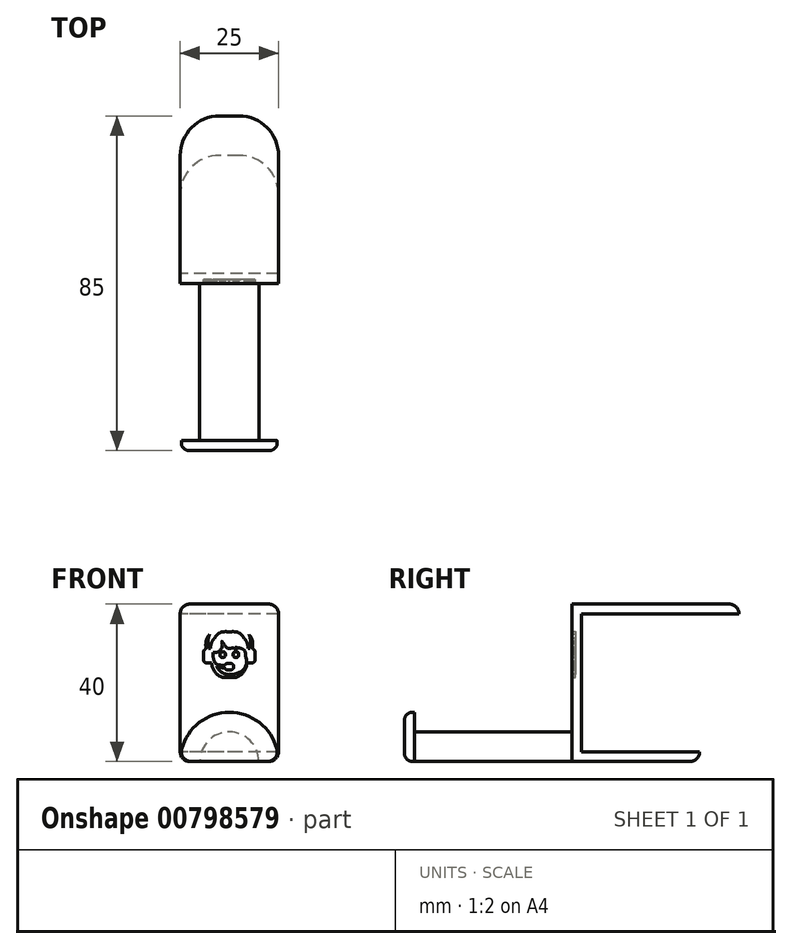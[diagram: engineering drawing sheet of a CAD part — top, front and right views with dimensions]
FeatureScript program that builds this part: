
annotation { "Feature Type Name" : "Feature", "Feature Type Description" : "" }
export const myFeature = defineFeature(function(context is Context, id is Id, definition is map)
    precondition{}
    {
        {
            var Q0;
            Q0=qCreatedBy(makeId("Right.planeOp"),FACE);
            var sketch = newSketch(context, id + "F0", { "sketchPlane" : qUnion([Q0])});
            skLineSegment(sketch, "E0", {"start": v(0, 0) * mm, "end": v(0, 35) * mm});
            skLineSegment(sketch, "E1", {"start": v(0, 35) * mm, "end": v(40, 35) * mm});
            skLineSegment(sketch, "E2", {"start": v(0, 0) * mm, "end": v(30, 0) * mm});
            skLineSegment(sketch, "E3.0", {"start": v(-2.5, 37.5) * mm, "end": v(40, 37.5) * mm});
            skLineSegment(sketch, "E3.1", {"start": v(-2.5, -2.5) * mm, "end": v(-2.5, 37.5) * mm});
            skLineSegment(sketch, "E3.2", {"start": v(-2.5, -2.5) * mm, "end": v(30, -2.5) * mm});
            skLineSegment(sketch, "E4", {"start": v(30, 0) * mm, "end": v(30, -2.5) * mm});
            skLineSegment(sketch, "E5", {"start": v(40, 35) * mm, "end": v(40, 37.5) * mm});
            skSolve(sketch);
        }
        {
            var Q0;
            Q0=makeQuery(id+"F0.imprint","IMPRINT",FACE,{"disambiguationData":[TD([[makeQuery(id+"F0.imprint","IMPRINT",EDGE,{"derivedFrom":sQuery(id+"F0.wireOp",EDGE,"E0")}),1.0]])]});
            extrude(context, id + "F1", {"entities" : qUnion([Q0]), "depth" : 25 * mm, "offsetDistance" : 25 * mm});
        }
        {
            var Q0;
            Q0=makeQuery(id+"F1.opExtrude","CAP_EDGE",EDGE,{"disambiguationData":[OSD([sQuery(id+"F0.wireOp",EDGE,"E5")])],"isStart":true});
            var Q1;
            Q1=makeQuery(id+"F1.opExtrude","CAP_EDGE",EDGE,{"disambiguationData":[OSD([sQuery(id+"F0.wireOp",EDGE,"E5")])],"isStart":false});
            var Q2;
            Q2=makeQuery(id+"F1.opExtrude","CAP_EDGE",EDGE,{"disambiguationData":[OSD([sQuery(id+"F0.wireOp",EDGE,"E4")])],"isStart":false});
            var Q3;
            Q3=makeQuery(id+"F1.opExtrude","CAP_EDGE",EDGE,{"disambiguationData":[OSD([sQuery(id+"F0.wireOp",EDGE,"E4")])],"isStart":true});
            fillet(context, id + "F2", {"entities" : qUnion([Q0, Q1, Q2, Q3]), "radius" : 10 * mm, "tangentPropagation" : true, "allowEdgeOverflow" : false});
        }
        {
            var Q0;
            Q0=makeQuery(id+"F2.opFillet","BLEND_EDGE",EDGE,{"blendedFrom":[makeQuery(id+"F1.opExtrude","CAP_EDGE",EDGE,{"disambiguationData":[OSD([sQuery(id+"F0.wireOp",EDGE,"E5")])],"isStart":true}),makeQuery(id+"F1.opExtrude","SWEPT_FACE",FACE,{"disambiguationData":[OSD([sQuery(id+"F0.wireOp",EDGE,"E3.0")])]})],"blendedInto":[makeQuery(id+"F1.opExtrude","SWEPT_FACE",FACE,{"disambiguationData":[OSD([sQuery(id+"F0.wireOp",EDGE,"E3.0")])]})]});
            var Q1;
            Q1=makeQuery(id+"F1.opExtrude","SWEPT_EDGE",EDGE,{"disambiguationData":[OSD([sQuery(id+"F0.wireOp",EDGE,"E3.0"),sQuery(id+"F0.wireOp",EDGE,"E5")])]});
            var Q2;
            Q2=makeQuery(id+"F2.opFillet","BLEND_EDGE",EDGE,{"blendedFrom":[makeQuery(id+"F1.opExtrude","CAP_EDGE",EDGE,{"disambiguationData":[OSD([sQuery(id+"F0.wireOp",EDGE,"E5")])],"isStart":false}),makeQuery(id+"F1.opExtrude","SWEPT_FACE",FACE,{"disambiguationData":[OSD([sQuery(id+"F0.wireOp",EDGE,"E3.0")])]})],"blendedInto":[makeQuery(id+"F1.opExtrude","SWEPT_FACE",FACE,{"disambiguationData":[OSD([sQuery(id+"F0.wireOp",EDGE,"E3.0")])]})]});
            var Q3;
            Q3=makeQuery(id+"F2.opFillet","BLEND_EDGE",EDGE,{"blendedFrom":[makeQuery(id+"F1.opExtrude","CAP_EDGE",EDGE,{"disambiguationData":[OSD([sQuery(id+"F0.wireOp",EDGE,"E4")])],"isStart":true}),makeQuery(id+"F1.opExtrude","SWEPT_FACE",FACE,{"disambiguationData":[OSD([sQuery(id+"F0.wireOp",EDGE,"E3.2")])]})],"blendedInto":[makeQuery(id+"F1.opExtrude","SWEPT_FACE",FACE,{"disambiguationData":[OSD([sQuery(id+"F0.wireOp",EDGE,"E3.2")])]})]});
            var Q4;
            Q4=makeQuery(id+"F1.opExtrude","SWEPT_EDGE",EDGE,{"disambiguationData":[OSD([sQuery(id+"F0.wireOp",EDGE,"E3.2"),sQuery(id+"F0.wireOp",EDGE,"E4")])]});
            var Q5;
            Q5=makeQuery(id+"F2.opFillet","BLEND_EDGE",EDGE,{"blendedFrom":[makeQuery(id+"F1.opExtrude","CAP_EDGE",EDGE,{"disambiguationData":[OSD([sQuery(id+"F0.wireOp",EDGE,"E4")])],"isStart":false}),makeQuery(id+"F1.opExtrude","SWEPT_FACE",FACE,{"disambiguationData":[OSD([sQuery(id+"F0.wireOp",EDGE,"E3.2")])]})],"blendedInto":[makeQuery(id+"F1.opExtrude","SWEPT_FACE",FACE,{"disambiguationData":[OSD([sQuery(id+"F0.wireOp",EDGE,"E3.2")])]})]});
            fillet(context, id + "F3", {"entities" : qUnion([Q0, Q1, Q2, Q3, Q4, Q5]), "radius" : 2.5 * mm, "tangentPropagation" : true, "allowEdgeOverflow" : false});
        }
        {
            var Q0;
            Q0=makeQuery(id+"F1.opExtrude","SWEPT_FACE",FACE,{"disambiguationData":[OSD([sQuery(id+"F0.wireOp",EDGE,"E3.1")])]});
            var sketch = newSketch(context, id + "F4", { "sketchPlane" : qUnion([Q0])});
            skCircle(sketch, "E6", {"center": v(12.5, -2.5) * mm, "radius": 7.5 * mm});
            skSolve(sketch);
        }
        {
            var Q0;
            {var subQ0=sQuery(id+"F4.wireOp",EDGE,"E6");var subQ1=makeQuery(id+"F1.opExtrude","SWEPT_EDGE",EDGE,{"disambiguationData":[OSD([sQuery(id+"F0.wireOp",EDGE,"E3.1"),sQuery(id+"F0.wireOp",EDGE,"E3.2")])]});var subQ2=makeQuery(id+"F4.imprint","INTERSECT",VERTEX,{"disambiguationData":[OD(0.0)],"derivedFrom":[subQ1,subQ0]});Q0=makeQuery(id+"F4.imprint","IMPRINT",FACE,{"disambiguationData":[TD([[makeQuery(id+"F4.imprint","IMPRINT",EDGE,{"disambiguationData":[TD([[subQ2,1.0]])],"derivedFrom":subQ0}),1.0]])]});}
            extrude(context, id + "F5", {"entities" : qUnion([Q0]), "operationType" : NewBodyOperationType.ADD, "depth" : 40 * mm, "offsetDistance" : 25 * mm});
        }
        {
            var Q0;
            Q0=makeQuery(id+"F5.opExtrude","CAP_FACE",FACE,{"disambiguationData":[OSD([sQuery(id+"F0.wireOp",EDGE,"E3.1"),sQuery(id+"F0.wireOp",EDGE,"E3.2"),sQuery(id+"F4.wireOp",EDGE,"E6")])],"isStart":false});
            var sketch = newSketch(context, id + "F6", { "sketchPlane" : qUnion([Q0])});
            skCircle(sketch, "E7", {"center": v(12.5, -2.5) * mm, "radius": 12.5 * mm});
            skLineSegment(sketch, "E8", {"start": v(12.5, -2.5) * mm, "end": v(25, -2.5) * mm});
            skLineSegment(sketch, "E9", {"start": v(12.5, -2.5) * mm, "end": v(0, -2.5) * mm});
            skSolve(sketch);
        }
        {
            var Q0;
            {var subQ1=makeQuery(id+"F5.opExtrude","CAP_EDGE",EDGE,{"disambiguationData":[OSD([sQuery(id+"F4.wireOp",EDGE,"E6")])],"isStart":false});Q0=makeQuery(id+"F6.imprint","IMPRINT",FACE,{"disambiguationData":[TD([[makeQuery(id+"F6.imprint","IMPRINT",EDGE,{"derivedFrom":subQ1}),1.0]])]});}
            var Q1;
            {var subQ5=makeQuery(id+"F5.opExtrude","CAP_EDGE",EDGE,{"disambiguationData":[OSD([sQuery(id+"F4.wireOp",EDGE,"E6")])],"isStart":false});Q1=makeQuery(id+"F6.imprint","IMPRINT",FACE,{"disambiguationData":[TD([[makeQuery(id+"F6.imprint","IMPRINT",EDGE,{"derivedFrom":subQ5}),-1.0]])]});}
            extrude(context, id + "F7", {"entities" : qUnion([Q0, Q1]), "operationType" : NewBodyOperationType.ADD, "depth" : 2.5 * mm, "offsetDistance" : 25 * mm});
        }
        {
            var Q0;
            Q0=makeQuery(id+"F7.opExtrude","SWEPT_EDGE",EDGE,{"disambiguationData":[OSD([sQuery(id+"F6.wireOp",EDGE,"E7"),sQuery(id+"F6.wireOp",EDGE,"E9")])]});
            var Q1;
            Q1=makeQuery(id+"F7.opExtrude","SWEPT_EDGE",EDGE,{"disambiguationData":[OSD([sQuery(id+"F6.wireOp",EDGE,"E7"),sQuery(id+"F6.wireOp",EDGE,"E8")])]});
            fillet(context, id + "F8", {"entities" : qUnion([Q0, Q1]), "radius" : 2.5 * mm, "tangentPropagation" : true, "allowEdgeOverflow" : false});
        }
        {
            var Q0;
            Q0=makeQuery(id+"F7.opExtrude","CAP_EDGE",EDGE,{"disambiguationData":[OSD([sQuery(id+"F6.wireOp",EDGE,"E7")])],"isStart":false});
            var Q1;
            Q1=makeQuery(id+"F5.opExtrude","CAP_EDGE",EDGE,{"disambiguationData":[OSD([sQuery(id+"F4.wireOp",EDGE,"E6")])],"isStart":false});
            var Q2;
            Q2=makeQuery(id+"F5.opExtrude","CAP_EDGE",EDGE,{"disambiguationData":[OSD([sQuery(id+"F4.wireOp",EDGE,"E6")])],"isStart":true});
            fillet(context, id + "F9", {"entities" : qUnion([Q0, Q1, Q2]), "radius" : 2 * mm, "tangentPropagation" : true, "allowEdgeOverflow" : false});
        }
        {
            var Q0;
            Q0=makeQuery(id+"F1.opExtrude","SWEPT_FACE",FACE,{"disambiguationData":[OSD([sQuery(id+"F0.wireOp",EDGE,"E3.1")])]});
            var sketch = newSketch(context, id + "F10", { "sketchPlane" : qUnion([Q0])});
            skFitSpline(sketch, "E10", {"points": [v(11.46, 24.67) * mm, v(11.46, 24.3) * mm, v(11.16, 24) * mm, v(10.8, 24) * mm]});
            skFitSpline(sketch, "E11", {"points": [v(10.8, 24) * mm, v(10.42, 24) * mm, v(10.12, 24.3) * mm, v(10.12, 24.67) * mm]});
            skFitSpline(sketch, "E12", {"points": [v(10.12, 24.67) * mm, v(10.12, 25.04) * mm, v(10.42, 25.34) * mm, v(10.8, 25.34) * mm]});
            skFitSpline(sketch, "E13", {"points": [v(10.8, 25.34) * mm, v(11.16, 25.34) * mm, v(11.46, 25.04) * mm, v(11.46, 24.67) * mm]});
            skFitSpline(sketch, "E14", {"points": [v(14.2, 25.34) * mm, v(13.82, 25.34) * mm, v(13.52, 25.04) * mm, v(13.52, 24.67) * mm]});
            skFitSpline(sketch, "E15", {"points": [v(13.52, 24.67) * mm, v(13.52, 24.3) * mm, v(13.82, 24) * mm, v(14.2, 24) * mm]});
            skFitSpline(sketch, "E16", {"points": [v(14.2, 24) * mm, v(14.56, 24) * mm, v(14.86, 24.3) * mm, v(14.86, 24.67) * mm]});
            skFitSpline(sketch, "E17", {"points": [v(14.86, 24.67) * mm, v(14.86, 25.04) * mm, v(14.56, 25.34) * mm, v(14.2, 25.34) * mm]});
            skLineSegment(sketch, "E18", {"start": v(19.03, 25.04) * mm, "end": v(19.03, 23.76) * mm});
            skFitSpline(sketch, "E19", {"points": [v(19.03, 23.76) * mm, v(19.03, 23.12) * mm, v(18.51, 22.6) * mm, v(17.87, 22.6) * mm]});
            skLineSegment(sketch, "E20", {"start": v(17.87, 22.6) * mm, "end": v(17.03, 22.6) * mm});
            skFitSpline(sketch, "E21", {"points": [v(17.03, 22.6) * mm, v(16.2, 20.29) * mm, v(14.07, 18.89) * mm, v(12.5, 18.89) * mm]});
            skFitSpline(sketch, "E22", {"points": [v(12.5, 18.89) * mm, v(10.92, 18.89) * mm, v(8.79, 20.29) * mm, v(7.95, 22.6) * mm]});
            skLineSegment(sketch, "E23", {"start": v(7.95, 22.6) * mm, "end": v(7.11, 22.6) * mm});
            skFitSpline(sketch, "E24", {"points": [v(7.11, 22.6) * mm, v(6.47, 22.6) * mm, v(5.95, 23.12) * mm, v(5.95, 23.76) * mm]});
            skLineSegment(sketch, "E25", {"start": v(5.95, 23.76) * mm, "end": v(5.95, 25.04) * mm});
            skFitSpline(sketch, "E26", {"points": [v(5.95, 25.04) * mm, v(5.95, 25.48) * mm, v(6.2, 25.87) * mm, v(6.56, 26.06) * mm]});
            skFitSpline(sketch, "E27", {"points": [v(6.56, 26.06) * mm, v(6.57, 27.87) * mm, v(7.1, 29.29) * mm, v(8.13, 30.27) * mm]});
            skFitSpline(sketch, "E28", {"points": [v(8.13, 30.27) * mm, v(9.16, 31.24) * mm, v(10.62, 31.73) * mm, v(12.5, 31.73) * mm]});
            skFitSpline(sketch, "E29", {"points": [v(12.5, 31.73) * mm, v(14.36, 31.73) * mm, v(15.83, 31.24) * mm, v(16.85, 30.27) * mm]});
            skFitSpline(sketch, "E30", {"points": [v(16.85, 30.27) * mm, v(17.88, 29.29) * mm, v(18.41, 27.87) * mm, v(18.42, 26.06) * mm]});
            skFitSpline(sketch, "E31", {"points": [v(18.42, 26.06) * mm, v(18.79, 25.87) * mm, v(19.03, 25.48) * mm, v(19.03, 25.04) * mm]});
            skFitSpline(sketch, "E32", {"points": [v(16.58, 24.66) * mm, v(16.58, 24.96) * mm, v(16.56, 25.24) * mm, v(16.54, 25.51) * mm]});
            skFitSpline(sketch, "E33", {"points": [v(16.54, 25.51) * mm, v(16.02, 25.98) * mm, v(15.09, 26.34) * mm, v(13.9, 26.47) * mm]});
            skFitSpline(sketch, "E34", {"points": [v(13.9, 26.47) * mm, v(14.06, 26.3) * mm, v(14.2, 26.07) * mm, v(14.28, 25.77) * mm]});
            skFitSpline(sketch, "E35", {"points": [v(14.28, 25.77) * mm, v(13.56, 26.34) * mm, v(12.14, 26.2) * mm, v(11.06, 27.48) * mm]});
            skFitSpline(sketch, "E36", {"points": [v(11.06, 27.48) * mm, v(11, 27.55) * mm, v(10.95, 27.62) * mm, v(10.9, 27.68) * mm]});
            skFitSpline(sketch, "E37", {"points": [v(10.9, 27.68) * mm, v(10.9, 27.68) * mm, v(10.9, 27.68) * mm, v(10.9, 27.68) * mm]});
            skLineSegment(sketch, "E38", {"start": v(10.9, 27.68) * mm, "end": v(10.9, 27.68) * mm});
            skFitSpline(sketch, "E39", {"points": [v(10.9, 27.68) * mm, v(10.71, 27.94) * mm, v(10.65, 28.1) * mm, v(10.64, 27.92) * mm]});
            skFitSpline(sketch, "E40", {"points": [v(10.64, 27.92) * mm, v(10.61, 26.46) * mm, v(9.57, 25.32) * mm, v(8.42, 25.16) * mm]});
            skFitSpline(sketch, "E41", {"points": [v(8.42, 25.16) * mm, v(8.41, 25) * mm, v(8.4, 24.83) * mm, v(8.4, 24.66) * mm]});
            skFitSpline(sketch, "E42", {"points": [v(8.4, 24.66) * mm, v(8.4, 24.04) * mm, v(8.5, 23.48) * mm, v(8.68, 22.97) * mm]});
            skFitSpline(sketch, "E43", {"points": [v(8.68, 22.97) * mm, v(9.33, 22.19) * mm, v(10.4, 21.97) * mm, v(11.34, 21.91) * mm]});
            skFitSpline(sketch, "E44", {"points": [v(11.34, 21.91) * mm, v(11.52, 22.2) * mm, v(11.91, 22.39) * mm, v(12.37, 22.39) * mm]});
            skFitSpline(sketch, "E45", {"points": [v(12.37, 22.39) * mm, v(13, 22.39) * mm, v(13.5, 22.03) * mm, v(13.5, 21.59) * mm]});
            skFitSpline(sketch, "E46", {"points": [v(13.5, 21.59) * mm, v(13.5, 21.14) * mm, v(13, 20.79) * mm, v(12.37, 20.79) * mm]});
            skFitSpline(sketch, "E47", {"points": [v(12.37, 20.79) * mm, v(11.9, 20.79) * mm, v(11.49, 21) * mm, v(11.32, 21.3) * mm]});
            skFitSpline(sketch, "E48", {"points": [v(11.32, 21.3) * mm, v(10.66, 21.34) * mm, v(9.93, 21.45) * mm, v(9.29, 21.75) * mm]});
            skFitSpline(sketch, "E49", {"points": [v(9.29, 21.75) * mm, v(10.2, 20.41) * mm, v(11.61, 19.7) * mm, v(12.5, 19.7) * mm]});
            skFitSpline(sketch, "E50", {"points": [v(12.5, 19.7) * mm, v(13.88, 19.7) * mm, v(16.58, 21.45) * mm, v(16.58, 24.66) * mm]});
            skLineSegment(sketch, "E51", {"start": v(16.58, 24.66) * mm, "end": v(16.58, 24.66) * mm});
            skFitSpline(sketch, "E52", {"points": [v(17.73, 26.2) * mm, v(17.65, 29.36) * mm, v(15.85, 31.03) * mm, v(12.5, 31.03) * mm]});
            skFitSpline(sketch, "E53", {"points": [v(12.5, 31.03) * mm, v(9.14, 31.03) * mm, v(7.33, 29.36) * mm, v(7.26, 26.2) * mm]});
            skLineSegment(sketch, "E54", {"start": v(7.26, 26.2) * mm, "end": v(7.7, 26.2) * mm});
            skFitSpline(sketch, "E55", {"points": [v(7.7, 26.2) * mm, v(7.87, 27.27) * mm, v(8.21, 28.14) * mm, v(8.74, 28.82) * mm]});
            skFitSpline(sketch, "E56", {"points": [v(8.74, 28.82) * mm, v(9.57, 29.9) * mm, v(10.84, 30.44) * mm, v(12.5, 30.44) * mm]});
            skFitSpline(sketch, "E57", {"points": [v(12.5, 30.44) * mm, v(14.15, 30.44) * mm, v(15.41, 29.9) * mm, v(16.25, 28.82) * mm]});
            skFitSpline(sketch, "E58", {"points": [v(16.25, 28.82) * mm, v(16.77, 28.14) * mm, v(17.12, 27.27) * mm, v(17.28, 26.2) * mm]});
            skLineSegment(sketch, "E59", {"start": v(17.28, 26.2) * mm, "end": v(17.73, 26.2) * mm});
            skSolve(sketch);
        }
        {
            var Q0;
            Q0=makeQuery(id+"F10.imprint","IMPRINT",FACE,{"disambiguationData":[TD([[makeQuery(id+"F10.imprint","IMPRINT",EDGE,{"derivedFrom":sQuery(id+"F10.wireOp",EDGE,"E18")}),-1.0]])]});
            var Q1;
            Q1=makeQuery(id+"F10.imprint","IMPRINT",FACE,{"disambiguationData":[TD([[makeQuery(id+"F10.imprint","IMPRINT",EDGE,{"derivedFrom":sQuery(id+"F10.wireOp",EDGE,"E14")}),1.0]])]});
            var Q2;
            Q2=makeQuery(id+"F10.imprint","IMPRINT",FACE,{"disambiguationData":[TD([[makeQuery(id+"F10.imprint","IMPRINT",EDGE,{"derivedFrom":sQuery(id+"F10.wireOp",EDGE,"E10")}),-1.0]])]});
            extrude(context, id + "F11", {"entities" : qUnion([Q0, Q1, Q2]), "operationType" : NewBodyOperationType.REMOVE, "oppositeDirection" : true, "depth" : 1 * mm, "offsetDistance" : 25 * mm});
        }
    });
